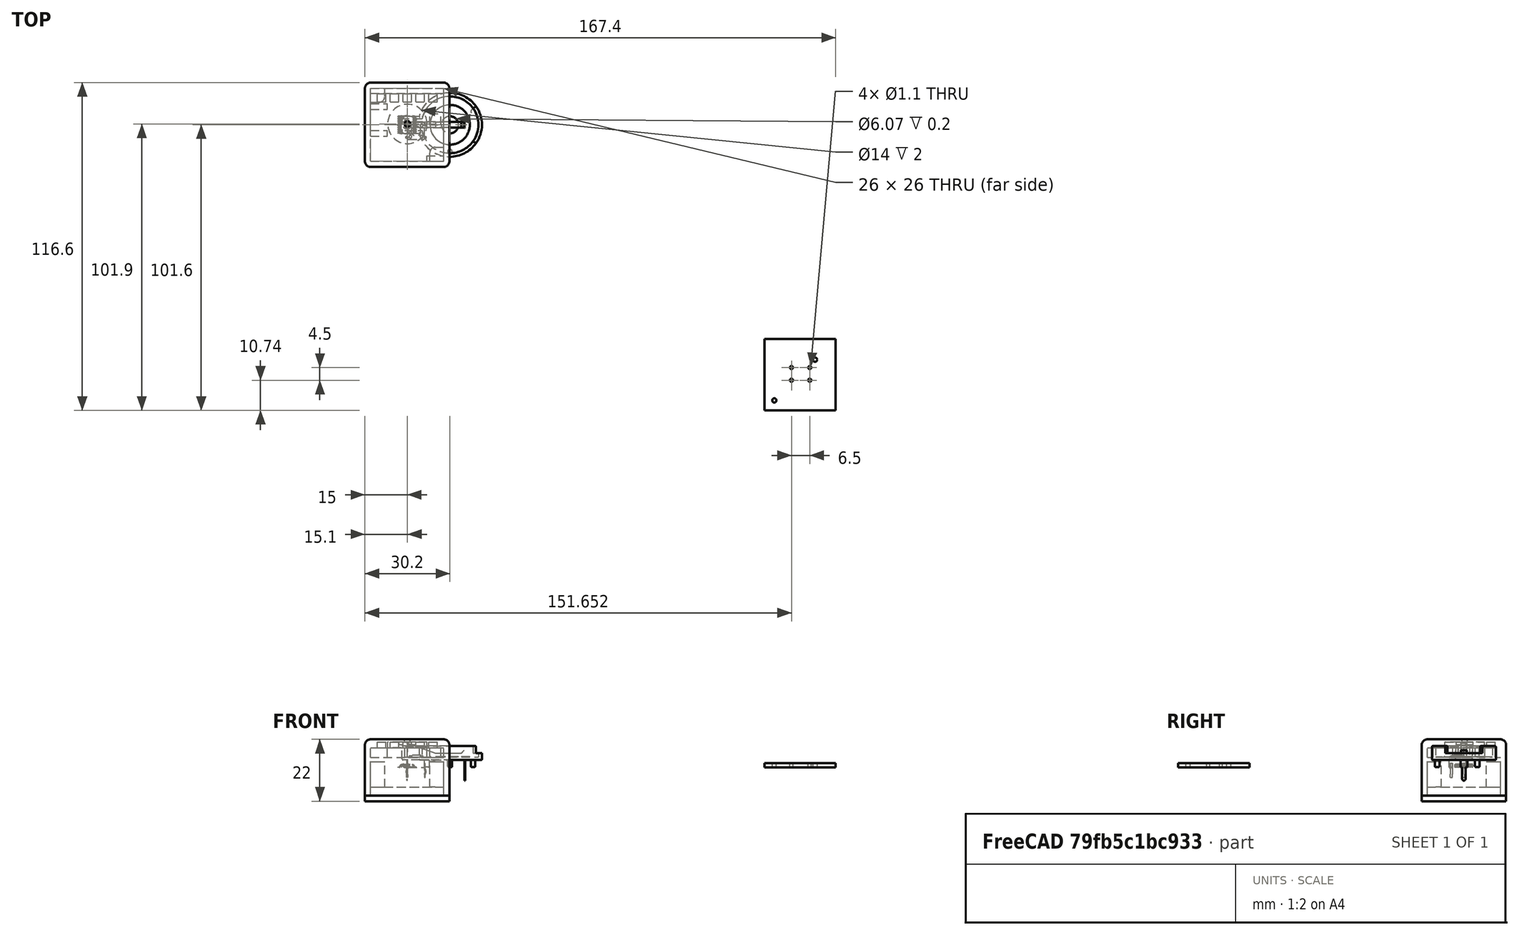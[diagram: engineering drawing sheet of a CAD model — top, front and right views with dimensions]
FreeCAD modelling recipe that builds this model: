
FCSTD DOCUMENT  (FreeCAD 0.17R13541 (Git))
Label: BoxSup
License: All rights reserved
LicenseURL: http://en.wikipedia.org/wiki/All_rights_reserved
objects: Part::Feature×30, App::Part×30, Part::Box×16, Part::MultiFuse×5, Part::Cut×4, Part::Cylinder×3, Part::Fillet×3
note: 61 computed .brp shape members not serialized (recipe doc carries the construction recipe); baked Part::Feature solids carry a one-line shape summary decoded from their .brp

FEATURE [Part::Box] Box  label="MainInside"
  AttacherType = Attacher::AttachEngine3D
  Height = 17
  Length = 26
  Placement = pos=(-13,-13,-10) rot=(0,0,1;0rad)
  Width = 26
FEATURE [Part::Box] Box001  label="MainOutside"
  AttacherType = Attacher::AttachEngine3D
  Height = 20
  Length = 30
  Placement = pos=(-15,-15,-10) rot=(0,0,1;0rad)
  Width = 30
FEATURE [Part::Feature] Part__Feature  label="SOLID"
  shape: bbox 2 x 1.25 x 1.1 mm, 50 faces (baked)
FEATURE [App::Part] LED_0805_2012Metric
  Group = -> [Part__Feature]
  License = CC BY 3.0
  LicenseURL = http://creativecommons.org/licenses/by/3.0/
  Origin = -> Origin
  Placement = pos=(144.272,-79.248,1.65) rot=(0,0,-1;1.5708rad)
FEATURE [Part::Feature] Part__Feature001  label="SOLID001"
  shape: bbox 7.174 x 6 x 7.8 mm, 105 faces (baked)
FEATURE [App::Part] SW_PUSH_6mm
  Group = -> [Part__Feature001]
  License = CC BY 3.0
  LicenseURL = http://creativecommons.org/licenses/by/3.0/
  Origin = -> Origin001
  Placement = pos=(136.652,-86.36,1.65) rot=(0,0,1;0rad)
FEATURE [Part::Feature] Part__Feature002  label="SOLID002"
  shape: bbox 1.6 x 0.8 x 0.45 mm, 26 faces (baked)
FEATURE [App::Part] R_0603_1608Metric
  Group = -> [Part__Feature002]
  License = CC BY 3.0
  LicenseURL = http://creativecommons.org/licenses/by/3.0/
  Origin = -> Origin002
  Placement = pos=(147.701,-98.679,1.65) rot=(0,0,1;0rad)
FEATURE [Part::Feature] Part__Feature003  label="SOLID003"
  shape: bbox 1.6 x 0.8 x 0.45 mm, 26 faces (baked)
FEATURE [App::Part] R_0603_1608Metric001
  Group = -> [Part__Feature003]
  License = CC BY 3.0
  LicenseURL = http://creativecommons.org/licenses/by/3.0/
  Origin = -> Origin003
  Placement = pos=(145.411,-99.187,1.65) rot=(0,0,1;1.5708rad)
FEATURE [Part::Feature] Part__Feature004  label="SOLID004"
  shape: bbox 6.4 x 6.5 x 1.2 mm, 336 faces (baked)
FEATURE [App::Part] TSSOP_20_4_4x6_5mm_P0_65mm
  Group = -> [Part__Feature004]
  License = CC BY 3.0
  LicenseURL = http://creativecommons.org/licenses/by/3.0/
  Origin = -> Origin004
  Placement = pos=(148.336,-93.81,1.65) rot=(0,0,1;1.5708rad)
FEATURE [Part::Feature] Part__Feature005  label="SOLID005"
  shape: bbox 2 x 1.25 x 1.1 mm, 50 faces (baked)
FEATURE [App::Part] LED_0805_2012Metric001
  Group = -> [Part__Feature005]
  License = CC BY 3.0
  LicenseURL = http://creativecommons.org/licenses/by/3.0/
  Origin = -> Origin005
  Placement = pos=(130.556,-79.248,1.65) rot=(0,0,-1;1.5708rad)
FEATURE [Part::Feature] Part__Feature006  label="SOLID006"
  shape: bbox 2 x 1.25 x 1.1 mm, 50 faces (baked)
FEATURE [App::Part] LED_0805_2012Metric002
  Group = -> [Part__Feature006]
  License = CC BY 3.0
  LicenseURL = http://creativecommons.org/licenses/by/3.0/
  Origin = -> Origin006
  Placement = pos=(135.128,-79.248,1.65) rot=(0,0,-1;1.5708rad)
FEATURE [Part::Feature] Part__Feature007  label="SOLID007"
  shape: bbox 2 x 1.25 x 1.1 mm, 50 faces (baked)
FEATURE [App::Part] LED_0805_2012Metric003
  Group = -> [Part__Feature007]
  License = CC BY 3.0
  LicenseURL = http://creativecommons.org/licenses/by/3.0/
  Origin = -> Origin007
  Placement = pos=(139.7,-79.248,1.65) rot=(0,0,-1;1.5708rad)
FEATURE [Part::Feature] Part__Feature008  label="SOLID008"
  shape: bbox 2 x 1.25 x 1.1 mm, 50 faces (baked)
FEATURE [App::Part] LED_0805_2012Metric004
  Group = -> [Part__Feature008]
  License = CC BY 3.0
  LicenseURL = http://creativecommons.org/licenses/by/3.0/
  Origin = -> Origin008
  Placement = pos=(148.844,-79.248,1.65) rot=(0,0,-1;1.5708rad)
FEATURE [Part::Feature] Part__Feature009  label="SOLID009"
  shape: bbox 1.6 x 0.8 x 0.45 mm, 26 faces (baked)
FEATURE [App::Part] R_0603_1608Metric002
  Group = -> [Part__Feature009]
  License = CC BY 3.0
  LicenseURL = http://creativecommons.org/licenses/by/3.0/
  Origin = -> Origin009
  Placement = pos=(132.588,-79.248,1.65) rot=(0,0,-1;1.5708rad)
FEATURE [Part::Feature] Part__Feature010  label="SOLID010"
  shape: bbox 1.6 x 0.8 x 0.45 mm, 26 faces (baked)
FEATURE [App::Part] R_0603_1608Metric003
  Group = -> [Part__Feature010]
  License = CC BY 3.0
  LicenseURL = http://creativecommons.org/licenses/by/3.0/
  Origin = -> Origin010
  Placement = pos=(137.16,-79.248,1.65) rot=(0,0,-1;1.5708rad)
FEATURE [Part::Feature] Part__Feature011  label="SOLID011"
  shape: bbox 1.6 x 0.8 x 0.45 mm, 26 faces (baked)
FEATURE [App::Part] R_0603_1608Metric004
  Group = -> [Part__Feature011]
  License = CC BY 3.0
  LicenseURL = http://creativecommons.org/licenses/by/3.0/
  Origin = -> Origin011
  Placement = pos=(141.732,-79.248,1.65) rot=(0,0,-1;1.5708rad)
FEATURE [Part::Feature] Part__Feature012  label="SOLID012"
  shape: bbox 1.6 x 0.8 x 0.45 mm, 26 faces (baked)
FEATURE [App::Part] R_0603_1608Metric005
  Group = -> [Part__Feature012]
  License = CC BY 3.0
  LicenseURL = http://creativecommons.org/licenses/by/3.0/
  Origin = -> Origin012
  Placement = pos=(146.304,-79.248,1.65) rot=(0,0,-1;1.5708rad)
FEATURE [Part::Feature] Part__Feature013  label="SOLID013"
  shape: bbox 1.6 x 0.8 x 0.45 mm, 26 faces (baked)
FEATURE [App::Part] R_0603_1608Metric006
  Group = -> [Part__Feature013]
  License = CC BY 3.0
  LicenseURL = http://creativecommons.org/licenses/by/3.0/
  Origin = -> Origin013
  Placement = pos=(150.876,-79.248,1.65) rot=(0,0,-1;1.5708rad)
FEATURE [Part::Feature] Part__Feature014  label="SOLID014"
  shape: bbox 1.6 x 0.8 x 0.8 mm, 28 faces (baked)
FEATURE [App::Part] C_0603_1608Metric
  Group = -> [Part__Feature014]
  License = CC BY 3.0
  LicenseURL = http://creativecommons.org/licenses/by/3.0/
  Origin = -> Origin014
  Placement = pos=(142.494,-94.488,1.65) rot=(0,0,-1;1.5708rad)
FEATURE [Part::Feature] Part__Feature015  label="SOLID015"
  shape: bbox 1.6 x 0.8 x 0.8 mm, 28 faces (baked)
FEATURE [App::Part] C_0603_1608Metric001
  Group = -> [Part__Feature015]
  License = CC BY 3.0
  LicenseURL = http://creativecommons.org/licenses/by/3.0/
  Origin = -> Origin015
  Placement = pos=(143.891,-94.488,1.65) rot=(0,0,-1;1.5708rad)
FEATURE [Part::Feature] Part__Feature016  label="SOLID016"
  shape: bbox 1.6 x 0.8 x 0.8 mm, 28 faces (baked)
FEATURE [App::Part] C_0603_1608Metric002
  Group = -> [Part__Feature016]
  License = CC BY 3.0
  LicenseURL = http://creativecommons.org/licenses/by/3.0/
  Origin = -> Origin016
  Placement = pos=(129.286,-95.631,1.65) rot=(0,0,1;0.785398rad)
FEATURE [Part::Feature] Part__Feature017  label="SOLID017"
  shape: bbox 1.6 x 0.8 x 0.8 mm, 28 faces (baked)
FEATURE [App::Part] C_0603_1608Metric003
  Group = -> [Part__Feature017]
  License = CC BY 3.0
  LicenseURL = http://creativecommons.org/licenses/by/3.0/
  Origin = -> Origin017
  Placement = pos=(128.778,-94.107,1.65) rot=(0,0,1;0.785398rad)
FEATURE [Part::Feature] Part__Feature018  label="SOLID018"
  shape: bbox 29.3 x 24.64 x 13.25 mm, 71 faces (baked)
FEATURE [App::Part] BatteryHolder_Keystone_103_1x20mm
  Group = -> [Part__Feature018]
  License = CC BY 3.0
  LicenseURL = http://creativecommons.org/licenses/by/3.0/
  Origin = -> Origin018
  Placement = pos=(130.556,-98.044,-0.05) rot=(0.92388,0.382683,0;3.14159rad)
FEATURE [Part::Feature] Part__Feature019  label="SOLID019"
  shape: bbox 2.5 x 3 x 1.2 mm, 76 faces (baked)
FEATURE [App::Part] SOT_23
  Group = -> [Part__Feature019]
  License = CC BY 3.0
  LicenseURL = http://creativecommons.org/licenses/by/3.0/
  Origin = -> Origin019
  Placement = pos=(130.81,-88.646,1.65) rot=(0,0,1;0rad)
FEATURE [Part::Feature] Part__Feature020  label="SOLID020"
  shape: bbox 2.5 x 3 x 1.2 mm, 76 faces (baked)
FEATURE [App::Part] SOT_23001
  Group = -> [Part__Feature020]
  License = CC BY 3.0
  LicenseURL = http://creativecommons.org/licenses/by/3.0/
  Origin = -> Origin020
  Placement = pos=(129.286,-85.09,1.65) rot=(0,0,1;3.14159rad)
FEATURE [Part::Feature] Part__Feature021  label="SOLID021"
  shape: bbox 1.6 x 0.8 x 0.45 mm, 26 faces (baked)
FEATURE [App::Part] R_0603_1608Metric007
  Group = -> [Part__Feature021]
  License = CC BY 3.0
  LicenseURL = http://creativecommons.org/licenses/by/3.0/
  Origin = -> Origin021
  Placement = pos=(128.27,-88.8745,1.65) rot=(0,0,1;1.5708rad)
FEATURE [Part::Feature] Part__Feature022  label="SOLID022"
  shape: bbox 1.6 x 0.8 x 0.45 mm, 26 faces (baked)
FEATURE [App::Part] R_0603_1608Metric008
  Group = -> [Part__Feature022]
  License = CC BY 3.0
  LicenseURL = http://creativecommons.org/licenses/by/3.0/
  Origin = -> Origin022
  Placement = pos=(131.699,-85.217,1.65) rot=(0,0,1;1.5708rad)
FEATURE [Part::Feature] Part__Feature023  label="SOLID023"
  shape: bbox 2.5 x 3 x 1.2 mm, 76 faces (baked)
FEATURE [App::Part] SOT_23002
  Group = -> [Part__Feature023]
  License = CC BY 3.0
  LicenseURL = http://creativecommons.org/licenses/by/3.0/
  Origin = -> Origin023
  Placement = pos=(135.89,-97.79,1.65) rot=(0,0,1;1.5708rad)
FEATURE [Part::Feature] Part__Feature024  label="SOLID024"
  shape: bbox 2.5 x 3 x 1.2 mm, 76 faces (baked)
FEATURE [App::Part] SOT_23003
  Group = -> [Part__Feature024]
  License = CC BY 3.0
  LicenseURL = http://creativecommons.org/licenses/by/3.0/
  Origin = -> Origin024
  Placement = pos=(139.446,-97.79,1.65) rot=(0,0,1;1.5708rad)
FEATURE [Part::Feature] Part__Feature025  label="SOLID025"
  shape: bbox 2.5 x 3 x 1.2 mm, 76 faces (baked)
FEATURE [App::Part] SOT_23004
  Group = -> [Part__Feature025]
  License = CC BY 3.0
  LicenseURL = http://creativecommons.org/licenses/by/3.0/
  Origin = -> Origin025
  Placement = pos=(143.002,-97.79,1.65) rot=(0,0,1;0rad)
FEATURE [Part::Feature] Part__Feature026  label="SOLID026"
  shape: bbox 1.6 x 0.8 x 0.45 mm, 26 faces (baked)
FEATURE [App::Part] R_0603_1608Metric009
  Group = -> [Part__Feature026]
  License = CC BY 3.0
  LicenseURL = http://creativecommons.org/licenses/by/3.0/
  Origin = -> Origin026
  Placement = pos=(135.89,-100.33,1.65) rot=(0,0,1;3.14159rad)
FEATURE [Part::Feature] Part__Feature027  label="SOLID027"
  shape: bbox 1.6 x 0.8 x 0.45 mm, 26 faces (baked)
FEATURE [App::Part] R_0603_1608Metric010
  Group = -> [Part__Feature027]
  License = CC BY 3.0
  LicenseURL = http://creativecommons.org/licenses/by/3.0/
  Origin = -> Origin027
  Placement = pos=(133.35,-99.5425,1.65) rot=(0,0,-1;1.5708rad)
FEATURE [Part::Feature] Part__Feature028  label="SOLID028"
  shape: bbox 1.6 x 0.8 x 0.45 mm, 26 faces (baked)
FEATURE [App::Part] R_0603_1608Metric011
  Group = -> [Part__Feature028]
  License = CC BY 3.0
  LicenseURL = http://creativecommons.org/licenses/by/3.0/
  Origin = -> Origin028
  Placement = pos=(139.192,-100.33,1.65) rot=(0,0,1;0rad)
FEATURE [Part::Feature] Part__Feature029  label="COMPOUND"
  shape: bbox 25.4 x 25.4 x 1.6 mm, 12 faces (baked)
FEATURE [App::Part] Open_CASCADE_STEP_translator_6_9_1
  Group = -> [LED_0805_2012Metric,SW_PUSH_6mm,R_0603_1608Metric,R_0603_1608Metric001,TSSOP_20_4_4x6_5mm_P0_65mm,LED_0805_2012Metric001,LED_0805_2012Metric002,LED_0805_2012Metric003,LED_0805_2012Metric004,R_0603_1608Metric002,R_0603_1608Metric003,R_0603_1608Metric004,R_0603_1608Metric005,R_0603_1608Metric006,C_0603_1608Metric,C_0603_1608Metric001,C_0603_1608Metric002,C_0603_1608Metric003,+12 more]
  License = CC BY 3.0
  LicenseURL = http://creativecommons.org/licenses/by/3.0/
  Origin = -> Origin029
  Placement = pos=(-139.7,88.9,2) rot=(0,0,1;0rad)
FEATURE [Part::Cut] Cut
  Base = -> Box001
  Tool = -> Box
FEATURE [Part::Box] Box002  label="L1"
  AttacherType = Attacher::AttachEngine3D
  Height = 2
  Length = 3
  Placement = pos=(-10.61,8.11,7) rot=(0,0,1;0rad)
  Width = 3
FEATURE [Part::Box] Box003  label="L2"
  AttacherType = Attacher::AttachEngine3D
  Height = 2
  Length = 3
  Placement = pos=(-6.04,8.11,7) rot=(0,0,1;0rad)
  Width = 3
FEATURE [Part::Box] Box004  label="L3"
  AttacherType = Attacher::AttachEngine3D
  Height = 2
  Length = 3
  Placement = pos=(-1.47,8.11,7) rot=(0,0,1;0rad)
  Width = 3
FEATURE [Part::Box] Box005  label="L4"
  AttacherType = Attacher::AttachEngine3D
  Height = 2
  Length = 3
  Placement = pos=(3.1,8.11,7) rot=(0,0,1;0rad)
  Width = 3
FEATURE [Part::Box] Box006  label="L5"
  AttacherType = Attacher::AttachEngine3D
  Height = 2
  Length = 3
  Placement = pos=(7.67,8.11,7) rot=(0,0,1;0rad)
  Width = 3
FEATURE [Part::Cylinder] Cylinder  label="But"
  Angle = 360
  AttacherType = Attacher::AttachEngine3D
  Height = 2
  Placement = pos=(0.1,0.3,7) rot=(0,0,1;0rad)
  Radius = 7
FEATURE [Part::Cylinder] Cylinder001  label="ButTouch"
  Angle = 360
  AttacherType = Attacher::AttachEngine3D
  Height = 2
  Placement = pos=(0.1,0.3,8) rot=(0,0,1;0rad)
  Radius = 3
FEATURE [Part::Cut] Cut001
  Base = -> Cut
  Tool = -> Cylinder
FEATURE [Part::MultiFuse] Fusion
  Shapes = -> [Box002,Box006,Box005,Box003,Box004]
FEATURE [Part::Cut] Cut002
  Base = -> Cut001
  Tool = -> Fusion
FEATURE [Part::MultiFuse] Fusion001
  Shapes = -> [Cylinder001,Cut002]
FEATURE [Part::Box] Box007  label="CubeDestek"
  AttacherType = Attacher::AttachEngine3D
  Height = 3.4
  Length = 26
  Placement = pos=(-13,11.2,3.6) rot=(0,0,1;0rad)
  Width = 1.8
FEATURE [Part::Box] Box008  label="CubeDestek2"
  AttacherType = Attacher::AttachEngine3D
  Height = 3.4
  Length = 4
  Placement = pos=(8,0,3.6) rot=(0,0,1;0rad)
  Width = 4
FEATURE [Part::Box] Box009  label="CubeDestek3"
  AttacherType = Attacher::AttachEngine3D
  Height = 3.4
  Length = 6
  Placement = pos=(-13,-4,3.6) rot=(0,0,1;0rad)
  Width = 2
FEATURE [Part::Box] Box010  label="CubeDestek4"
  AttacherType = Attacher::AttachEngine3D
  Height = 3.4
  Length = 6
  Placement = pos=(-13,5.5,3.6) rot=(0,0,1;0rad)
  Width = 2
FEATURE [Part::Box] Box011  label="CubeDestek5"
  AttacherType = Attacher::AttachEngine3D
  Height = 3.4
  Length = 6
  Placement = pos=(7,-13,3.6) rot=(0,0,1;0rad)
  Width = 2
FEATURE [Part::MultiFuse] Fusion002  label="FusionDestek"
  Shapes = -> [Box011,Box010,Box008,Box007,Box009]
FEATURE [Part::Box] Box012  label="KapakGenis"
  AttacherType = Attacher::AttachEngine3D
  Height = 2
  Length = 30
  Placement = pos=(-15,-15,-12) rot=(0,0,1;0rad)
  Width = 30
FEATURE [Part::Box] Box013  label="KapakIc"
  AttacherType = Attacher::AttachEngine3D
  Height = 3
  Length = 26
  Placement = pos=(-13,-13,-10) rot=(0,0,1;0rad)
  Width = 26
FEATURE [Part::Box] Box014  label="KapakCikinti1"
  AttacherType = Attacher::AttachEngine3D
  Height = 9
  Length = 5
  Placement = pos=(-13,8,-7) rot=(0,0,1;0rad)
  Width = 5
FEATURE [Part::Box] Box015  label="KapakCikinti2"
  AttacherType = Attacher::AttachEngine3D
  Height = 9
  Length = 5
  Placement = pos=(8,-13,-7) rot=(0,0,1;0rad)
  Width = 5
FEATURE [Part::Cylinder] Cylinder002  label="ButTouch001"
  Angle = 360
  AttacherType = Attacher::AttachEngine3D
  Height = 1
  Placement = pos=(0.1,0.3,9) rot=(0,0,1;0rad)
  Radius = 1
FEATURE [Part::Cut] Cut003
  Base = -> Fusion001
  Tool = -> Cylinder002
FEATURE [Part::MultiFuse] Fusion003  label="kutu"
  Shapes = -> [Fusion002,Cut003]
FEATURE [Part::MultiFuse] Fusion004  label="kapak"
  Shapes = -> [Box015,Box013,Box014,Box012]
FEATURE [Part::Fillet] Fillet
  Base = -> Fusion003
  Edges = 8 edges r=2: [Edge132,Edge133,Edge134,Edge135,Edge136,Edge137,Edge138,Edge139]
FEATURE [Part::Fillet] Fillet001
  Base = -> Fusion004
  Edges = 4 edges r=2: [Edge41,Edge42,Edge45,Edge47]
FEATURE [Part::Fillet] Fillet002
  Base = -> Fillet001
  Edges = 2 edges r=2: [Edge55,Edge58]
